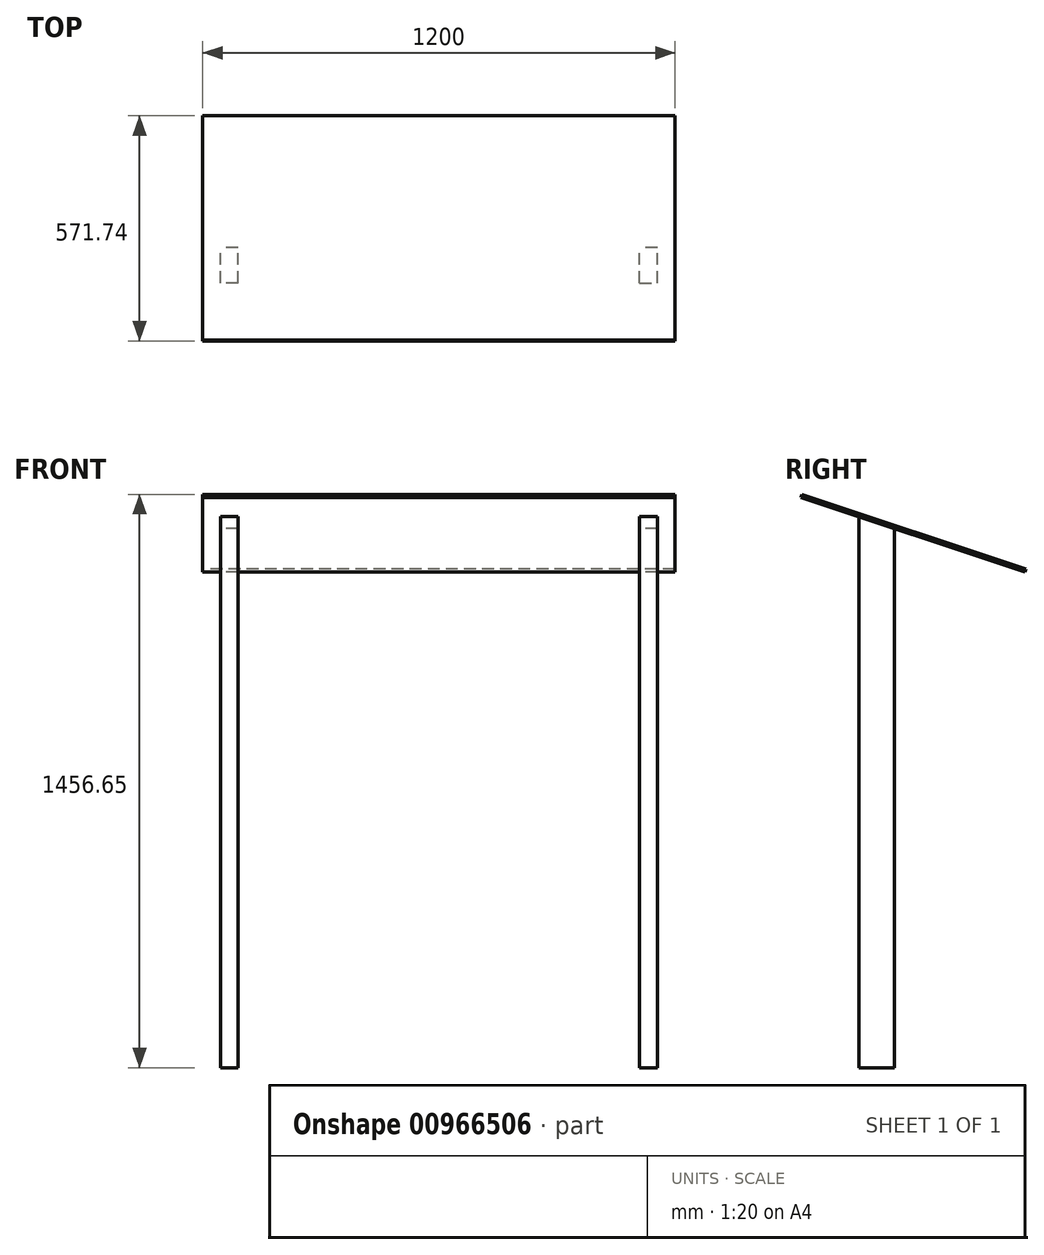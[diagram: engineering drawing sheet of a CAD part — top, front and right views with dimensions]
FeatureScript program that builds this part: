
annotation { "Feature Type Name" : "Feature", "Feature Type Description" : "" }
export const myFeature = defineFeature(function(context is Context, id is Id, definition is map)
    precondition{}
    {
        {
            var Q0;
            Q0=qCreatedBy(makeId("Top.planeOp"),FACE);
            var sketch = newSketch(context, id + "F0", { "sketchPlane" : qUnion([Q0])});
            skLineSegment(sketch, "E0", {"start": v(0, 0) * mm, "end": v(-510, 0) * mm, "construction": true});
            skLineSegment(sketch, "E1", {"start": v(0, 0) * mm, "end": v(510, 0) * mm, "construction": true});
            skLineSegment(sketch, "E2.bottom", {"start": v(-510, 0) * mm, "end": v(-555, 0) * mm});
            skLineSegment(sketch, "E2.top", {"start": v(-510, 90) * mm, "end": v(-555, 90) * mm});
            skLineSegment(sketch, "E2.left", {"start": v(-510, 0) * mm, "end": v(-510, 90) * mm});
            skLineSegment(sketch, "E2.right", {"start": v(-555, 0) * mm, "end": v(-555, 90) * mm});
            skLineSegment(sketch, "E3", {"start": v(0, 0) * mm, "end": v(0, 400) * mm, "construction": true});
            skLineSegment(sketch, "E4.MirrorCS", {"start": v(555, 0) * mm, "end": v(555, 90) * mm});
            skLineSegment(sketch, "E5.MirrorCS", {"start": v(510, 0) * mm, "end": v(510, 90) * mm});
            skLineSegment(sketch, "E6.MirrorCS", {"start": v(510, 0) * mm, "end": v(555, 0) * mm});
            skLineSegment(sketch, "E7.MirrorCS", {"start": v(510, 90) * mm, "end": v(555, 90) * mm});
            skSolve(sketch);
        }
        {
            var Q0;
            Q0 = qSketchRegion(id + "F0", true);
            extrude(context, id + "F1", {"entities" : qUnion([Q0]), "depth" : 1400 * mm, "offsetDistance" : 25 * mm});
        }
        {
            var Q0;
            Q0=makeQuery(id+"F1.opExtrude","SWEPT_FACE",FACE,{"disambiguationData":[OSD([sQuery(id+"F0.wireOp",EDGE,"E2.right")])]});
            var sketch = newSketch(context, id + "F2", { "sketchPlane" : qUnion([Q0])});
            skLineSegment(sketch, "E8", {"start": v(-90, 1400) * mm, "end": v(0, 1400) * mm});
            skLineSegment(sketch, "E9", {"start": v(0, 1400) * mm, "end": v(-90, 1370) * mm});
            skLineSegment(sketch, "E10", {"start": v(-90, 1370) * mm, "end": v(-90, 1400) * mm});
            skSolve(sketch);
        }
        {
            var Q0;
            Q0 = qSketchRegion(id + "F2", true);
            extrude(context, id + "F3", {"entities" : qUnion([Q0]), "operationType" : NewBodyOperationType.REMOVE, "endBound" : BoundingType.THROUGH_ALL, "oppositeDirection" : true, "depth" : 25 * mm, "offsetDistance" : 25 * mm});
        }
        {
            var Q0;
            Q0=makeQuery(id+"F1.opExtrude","SWEPT_FACE",FACE,{"disambiguationData":[OSD([sQuery(id+"F0.wireOp",EDGE,"E5.MirrorCS")])]});
            var sketch = newSketch(context, id + "F4", { "sketchPlane" : qUnion([Q0])});
            skLineSegment(sketch, "E11", {"start": v(-90, 1400) * mm, "end": v(0, 1400) * mm});
            skLineSegment(sketch, "E12", {"start": v(0, 1400) * mm, "end": v(-90, 1370) * mm});
            skLineSegment(sketch, "E13", {"start": v(-90, 1370) * mm, "end": v(-90, 1400) * mm});
            skSolve(sketch);
        }
        {
            var Q0;
            Q0 = qSketchRegion(id + "F4", true);
            extrude(context, id + "F5", {"entities" : qUnion([Q0]), "operationType" : NewBodyOperationType.REMOVE, "endBound" : BoundingType.THROUGH_ALL, "oppositeDirection" : true, "depth" : 25 * mm, "offsetDistance" : 25 * mm});
        }
        {
            var Q0;
            Q0=makeQuery(id+"F3.boolean.opBoolean","COPY",FACE,{"derivedFrom":makeQuery(id+"F3.opExtrude","SWEPT_FACE",FACE,{"disambiguationData":[OSD([sQuery(id+"F2.wireOp",EDGE,"E9")])]})});
            var sketch = newSketch(context, id + "F6", { "sketchPlane" : qUnion([Q0])});
            skLineSegment(sketch, "E14.bottom", {"start": v(600, 2.15) * mm, "end": v(-600, 2.15) * mm});
            skLineSegment(sketch, "E14.top", {"start": v(600, -597.85) * mm, "end": v(-600, -597.85) * mm});
            skLineSegment(sketch, "E14.left", {"start": v(600, 2.15) * mm, "end": v(600, -597.85) * mm});
            skLineSegment(sketch, "E14.right", {"start": v(-600, 2.15) * mm, "end": v(-600, -597.85) * mm});
            skSolve(sketch);
        }
        {
            var Q0;
            Q0 = qSketchRegion(id + "F6", true);
            extrude(context, id + "F7", {"entities" : qUnion([Q0]), "depth" : 8 * mm, "offsetDistance" : 25 * mm});
        }
    });
